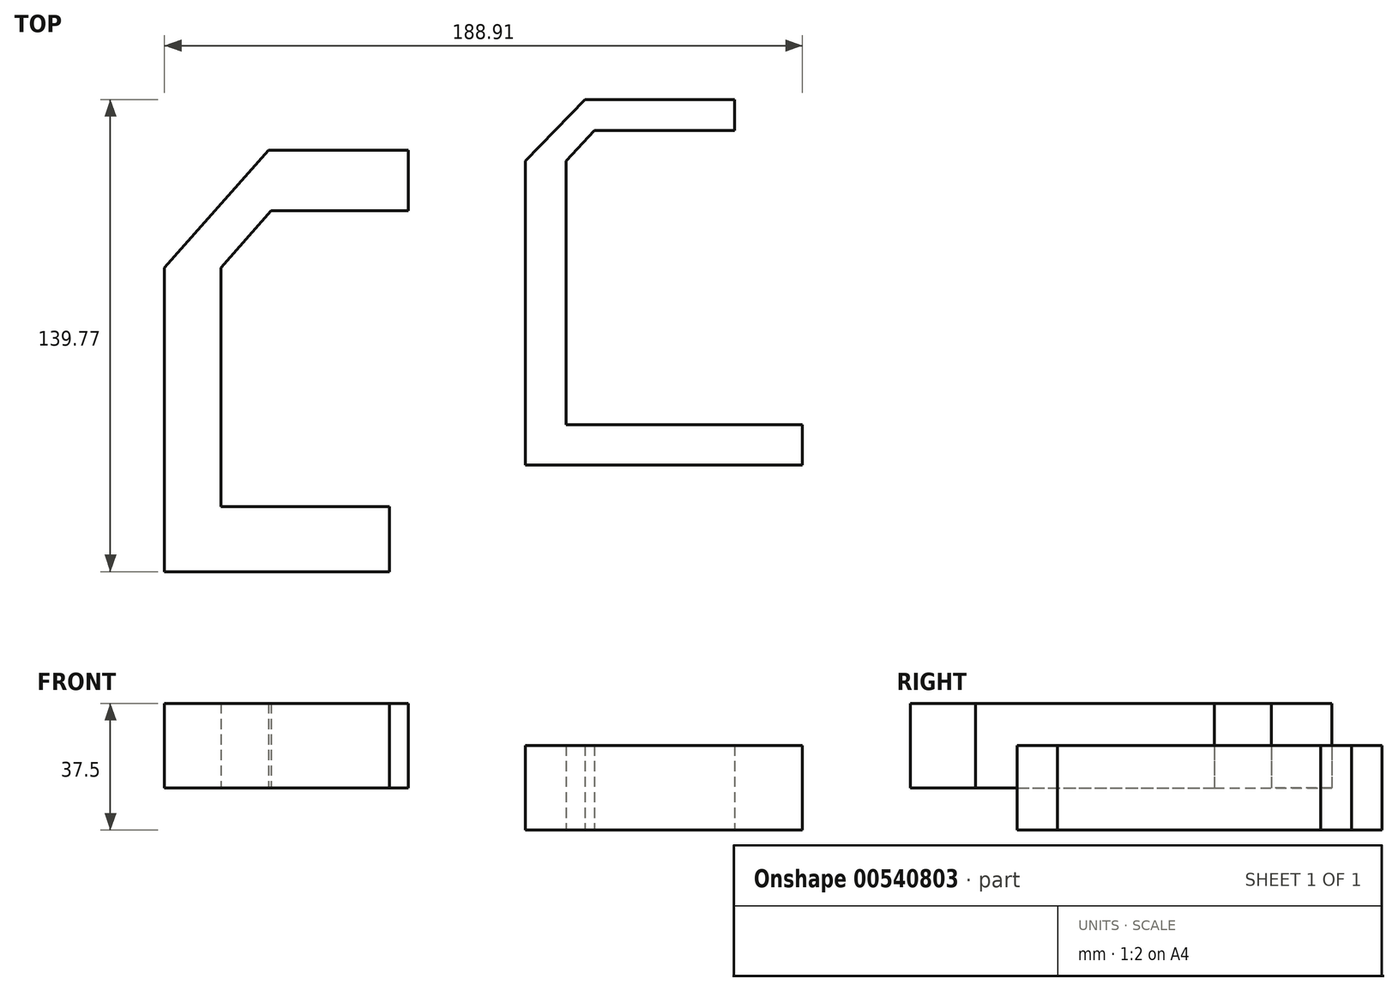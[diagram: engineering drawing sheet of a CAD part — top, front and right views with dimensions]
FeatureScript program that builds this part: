
annotation { "Feature Type Name" : "Feature", "Feature Type Description" : "" }
export const myFeature = defineFeature(function(context is Context, id is Id, definition is map)
    precondition{}
    {
        {
            var Q0;
            Q0=qCreatedBy(makeId("Top.planeOp"),FACE);
            var sketch = newSketch(context, id + "F0", { "sketchPlane" : qUnion([Q0])});
            skLineSegment(sketch, "E0.bottom", {"start": v(35, 6) * mm, "end": v(-35, 6) * mm});
            skLineSegment(sketch, "E0.top", {"start": v(35, -6) * mm, "end": v(-35, -6) * mm});
            skLineSegment(sketch, "E0.left", {"start": v(35, 6) * mm, "end": v(35, -6) * mm});
            skLineSegment(sketch, "E0.right", {"start": v(-35, 6) * mm, "end": v(-35, -6) * mm});
            skPoint(sketch, "E0.middle", {"position": v(0, 0) * mm});
            skLineSegment(sketch, "E1.bottom", {"start": v(-35, -6) * mm, "end": v(-47, -6) * mm});
            skLineSegment(sketch, "E1.top", {"start": v(-35, 84) * mm, "end": v(-47, 84) * mm});
            skLineSegment(sketch, "E1.left", {"start": v(-35, -6) * mm, "end": v(-35, 84) * mm});
            skLineSegment(sketch, "E1.right", {"start": v(-47, -6) * mm, "end": v(-47, 84) * mm});
            skPoint(sketch, "E1.middle", {"position": v(-41, 39) * mm});
            skLineSegment(sketch, "E2", {"start": v(-47, 84) * mm, "end": v(-29.41, 102.2) * mm});
            skLineSegment(sketch, "E3", {"start": v(-35, 84) * mm, "end": v(-23.84, 96.03) * mm});
            skPoint(sketch, "E4.oppositeSnap0", {"position": v(-38.2, 93.1) * mm});
            skLineSegment(sketch, "E4.bottom", {"start": v(-29.41, 102.2) * mm, "end": v(15, 102.2) * mm});
            skLineSegment(sketch, "E4.top", {"start": v(-29.41, 93.1) * mm, "end": v(15, 93.1) * mm});
            skLineSegment(sketch, "E4.left", {"start": v(-29.41, 102.2) * mm, "end": v(-29.41, 93.1) * mm});
            skLineSegment(sketch, "E4.right", {"start": v(15, 102.2) * mm, "end": v(15, 93.1) * mm});
            skSolve(sketch);
        }
        {
            var Q0;
            Q0 = qSketchRegion(id + "F0", true);
            extrude(context, id + "F1", {"entities" : qUnion([Q0]), "endBound" : BoundingType.SYMMETRIC, "depth" : 25 * mm, "offsetDistance" : 25 * mm});
        }
        {
            var Q0;
            Q0=qCreatedBy(makeId("Top.planeOp"),FACE);
            var sketch = newSketch(context, id + "F2", { "sketchPlane" : qUnion([Q0])});
            skLineSegment(sketch, "E5.bottom", {"start": v(-87.25, -18.26) * mm, "end": v(-137.25, -18.26) * mm});
            skLineSegment(sketch, "E5.top", {"start": v(-87.25, -37.57) * mm, "end": v(-137.25, -37.57) * mm});
            skLineSegment(sketch, "E5.left", {"start": v(-87.25, -18.26) * mm, "end": v(-87.25, -37.57) * mm});
            skLineSegment(sketch, "E5.right", {"start": v(-137.25, -18.26) * mm, "end": v(-137.25, -37.57) * mm});
            skPoint(sketch, "E5.middle", {"position": v(-112.25, -27.92) * mm});
            skLineSegment(sketch, "E6.bottom", {"start": v(-137.25, -37.57) * mm, "end": v(-153.91, -37.57) * mm});
            skLineSegment(sketch, "E6.top", {"start": v(-137.25, 52.43) * mm, "end": v(-153.91, 52.43) * mm});
            skLineSegment(sketch, "E6.left", {"start": v(-137.25, -37.57) * mm, "end": v(-137.25, 52.43) * mm});
            skLineSegment(sketch, "E6.right", {"start": v(-153.91, -37.57) * mm, "end": v(-153.91, 52.43) * mm});
            skPoint(sketch, "E6.middle", {"position": v(-145.58, 7.43) * mm});
            skLineSegment(sketch, "E7", {"start": v(-153.91, 52.43) * mm, "end": v(-123.11, 87.27) * mm});
            skLineSegment(sketch, "E8", {"start": v(-137.25, 52.43) * mm, "end": v(-122.31, 69.33) * mm});
            skLineSegment(sketch, "E9.bottom", {"start": v(-123.11, 87.27) * mm, "end": v(-81.74, 87.27) * mm});
            skLineSegment(sketch, "E9.top", {"start": v(-123.11, 69.33) * mm, "end": v(-81.74, 69.33) * mm});
            skLineSegment(sketch, "E9.left", {"start": v(-123.11, 87.27) * mm, "end": v(-123.11, 69.33) * mm});
            skLineSegment(sketch, "E9.right", {"start": v(-81.74, 87.27) * mm, "end": v(-81.74, 69.33) * mm});
            skPoint(sketch, "E10.orphan", {"position": v(-112.25, 80.7) * mm});
            skSolve(sketch);
        }
        {
            var Q0;
            Q0 = qSketchRegion(id + "F2", true);
            extrude(context, id + "F3", {"entities" : qUnion([Q0]), "depth" : 25 * mm, "offsetDistance" : 25 * mm});
        }
    });
